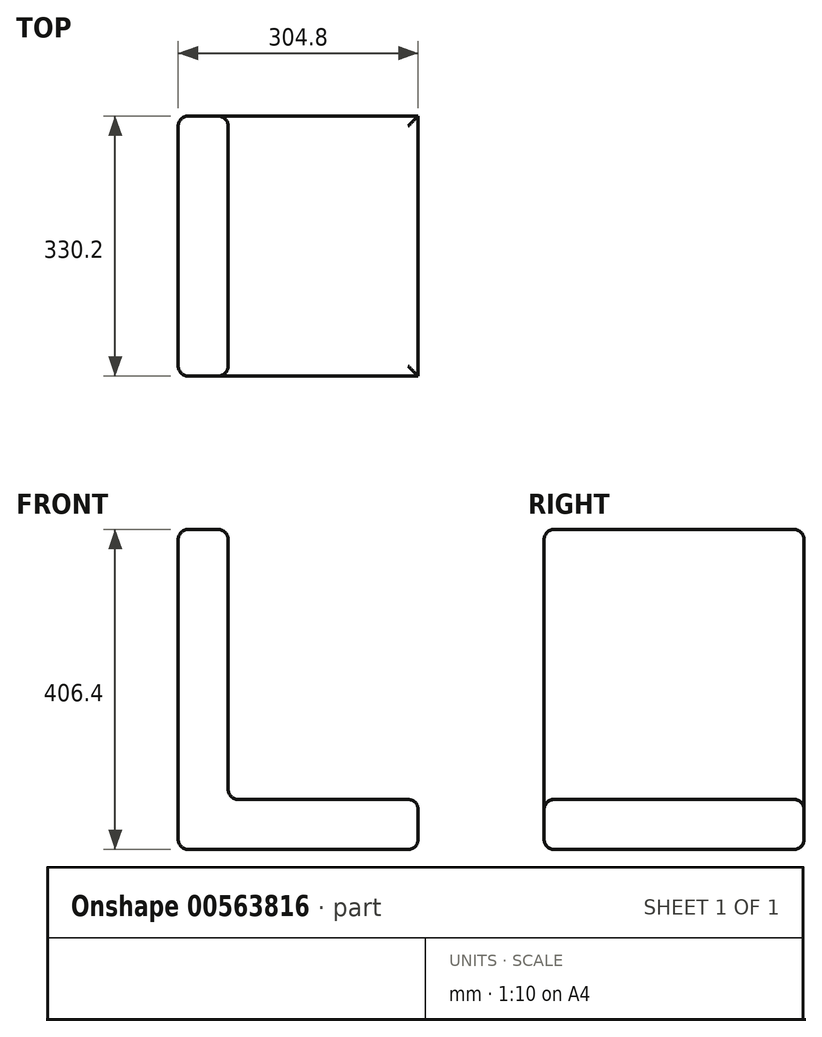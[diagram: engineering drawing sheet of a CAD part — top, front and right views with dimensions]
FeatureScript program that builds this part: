
annotation { "Feature Type Name" : "Feature", "Feature Type Description" : "" }
export const myFeature = defineFeature(function(context is Context, id is Id, definition is map)
    precondition{}
    {
        {
            var Q0;
            Q0=qCreatedBy(makeId("Front.planeOp"),FACE);
            var sketch = newSketch(context, id + "F0", { "sketchPlane" : qUnion([Q0])});
            skLineSegment(sketch, "E0.bottom", {"start": v(-152.4, 27.53) * mm, "end": v(152.4, 27.53) * mm});
            skLineSegment(sketch, "E0.top", {"start": v(-152.4, -35.97) * mm, "end": v(152.4, -35.97) * mm});
            skLineSegment(sketch, "E0.left", {"start": v(-152.4, 27.53) * mm, "end": v(-152.4, -35.97) * mm});
            skLineSegment(sketch, "E0.right", {"start": v(152.4, 27.53) * mm, "end": v(152.4, -35.97) * mm});
            skPoint(sketch, "E0.middle", {"position": v(0, -4.22) * mm});
            skLineSegment(sketch, "E1.bottom", {"start": v(-152.4, -35.97) * mm, "end": v(-88.9, -35.97) * mm});
            skLineSegment(sketch, "E1.top", {"start": v(-152.4, 370.43) * mm, "end": v(-88.9, 370.43) * mm});
            skLineSegment(sketch, "E1.left", {"start": v(-152.4, -35.97) * mm, "end": v(-152.4, 370.43) * mm});
            skLineSegment(sketch, "E1.right", {"start": v(-88.9, -35.97) * mm, "end": v(-88.9, 370.43) * mm});
            skSolve(sketch);
        }
        {
            var Q0;
            {var subQ5=sQuery(id+"F0.wireOp",EDGE,"E1.top");Q0=makeQuery(id+"F0.imprint","IMPRINT",FACE,{"disambiguationData":[TD([[makeQuery(id+"F0.imprint","IMPRINT",EDGE,{"derivedFrom":subQ5}),-1.0]])]});}
            var Q1;
            {var subQ5=sQuery(id+"F0.wireOp",EDGE,"E1.bottom");Q1=makeQuery(id+"F0.imprint","IMPRINT",FACE,{"disambiguationData":[TD([[makeQuery(id+"F0.imprint","IMPRINT",EDGE,{"derivedFrom":subQ5}),1.0]])]});}
            var Q2;
            {var subQ4=sQuery(id+"F0.wireOp",EDGE,"E0.top");Q2=makeQuery(id+"F0.imprint","IMPRINT",FACE,{"disambiguationData":[TD([[makeQuery(id+"F0.imprint","IMPRINT",EDGE,{"derivedFrom":subQ4}),1.0]])]});}
            extrude(context, id + "F1", {"entities" : qUnion([Q0, Q1, Q2]), "endBound" : BoundingType.SYMMETRIC, "depth" : 330.2 * mm, "offsetDistance" : 25.4 * mm});
        }
        {
            var Q0;
            Q0=makeQuery(id+"F1.opExtrude","CAP_EDGE",EDGE,{"disambiguationData":[OSD([sQuery(id+"F0.wireOp",EDGE,"E0.bottom")])],"isStart":false});
            var Q1;
            Q1=makeQuery(id+"F1.opExtrude","SWEPT_EDGE",EDGE,{"disambiguationData":[OSD([sQuery(id+"F0.wireOp",EDGE,"E0.bottom"),sQuery(id+"F0.wireOp",EDGE,"E0.right")])]});
            var Q2;
            Q2=makeQuery(id+"F1.opExtrude","CAP_EDGE",EDGE,{"disambiguationData":[OSD([sQuery(id+"F0.wireOp",EDGE,"E0.bottom")])],"isStart":true});
            var Q3;
            Q3=makeQuery(id+"F1.opExtrude","SWEPT_EDGE",EDGE,{"disambiguationData":[OSD([sQuery(id+"F0.wireOp",EDGE,"E0.bottom"),sQuery(id+"F0.wireOp",EDGE,"E1.right")])]});
            var Q4;
            Q4=makeQuery(id+"F1.opExtrude","CAP_EDGE",EDGE,{"disambiguationData":[OSD([sQuery(id+"F0.wireOp",EDGE,"E1.right")])],"isStart":true});
            var Q5;
            Q5=makeQuery(id+"F1.opExtrude","CAP_EDGE",EDGE,{"disambiguationData":[OSD([sQuery(id+"F0.wireOp",EDGE,"E1.right")])],"isStart":false});
            var Q6;
            Q6=makeQuery(id+"F1.opExtrude","SWEPT_EDGE",EDGE,{"disambiguationData":[OSD([sQuery(id+"F0.wireOp",EDGE,"E1.top"),sQuery(id+"F0.wireOp",EDGE,"E1.right")])]});
            fillet(context, id + "F2", {"entities" : qUnion([Q0, Q1, Q2, Q3, Q4, Q5, Q6]), "radius" : 12.7 * mm, "tangentPropagation" : true, "allowEdgeOverflow" : false});
        }
        {
            var Q0;
            Q0=makeQuery(id+"F1.opExtrude","CAP_EDGE",EDGE,{"disambiguationData":[OSD([sQuery(id+"F0.wireOp",EDGE,"E0.top"),sQuery(id+"F0.wireOp",EDGE,"E1.bottom")])],"isStart":false});
            var Q1;
            Q1=makeQuery(id+"F1.opExtrude","SWEPT_EDGE",EDGE,{"disambiguationData":[OSD([sQuery(id+"F0.wireOp",EDGE,"E0.top"),sQuery(id+"F0.wireOp",EDGE,"E0.right")])]});
            var Q2;
            Q2=makeQuery(id+"F1.opExtrude","CAP_EDGE",EDGE,{"disambiguationData":[OSD([sQuery(id+"F0.wireOp",EDGE,"E0.top"),sQuery(id+"F0.wireOp",EDGE,"E1.bottom")])],"isStart":true});
            var Q3;
            Q3=makeQuery(id+"F1.opExtrude","SWEPT_EDGE",EDGE,{"disambiguationData":[OSD([sQuery(id+"F0.wireOp",EDGE,"E1.bottom"),sQuery(id+"F0.wireOp",EDGE,"E1.left")])]});
            fillet(context, id + "F3", {"entities" : qUnion([Q0, Q1, Q2, Q3]), "radius" : 12.7 * mm, "tangentPropagation" : true, "allowEdgeOverflow" : false});
        }
        {
            var Q0;
            Q0=makeQuery(id+"F1.opExtrude","CAP_EDGE",EDGE,{"disambiguationData":[OSD([sQuery(id+"F0.wireOp",EDGE,"E1.left")])],"isStart":false});
            var Q1;
            Q1=makeQuery(id+"F1.opExtrude","SWEPT_EDGE",EDGE,{"disambiguationData":[OSD([sQuery(id+"F0.wireOp",EDGE,"E1.top"),sQuery(id+"F0.wireOp",EDGE,"E1.left")])]});
            var Q2;
            Q2=makeQuery(id+"F1.opExtrude","CAP_EDGE",EDGE,{"disambiguationData":[OSD([sQuery(id+"F0.wireOp",EDGE,"E1.left")])],"isStart":true});
            fillet(context, id + "F4", {"entities" : qUnion([Q0, Q1, Q2]), "radius" : 12.7 * mm, "tangentPropagation" : true, "allowEdgeOverflow" : false});
        }
    });
